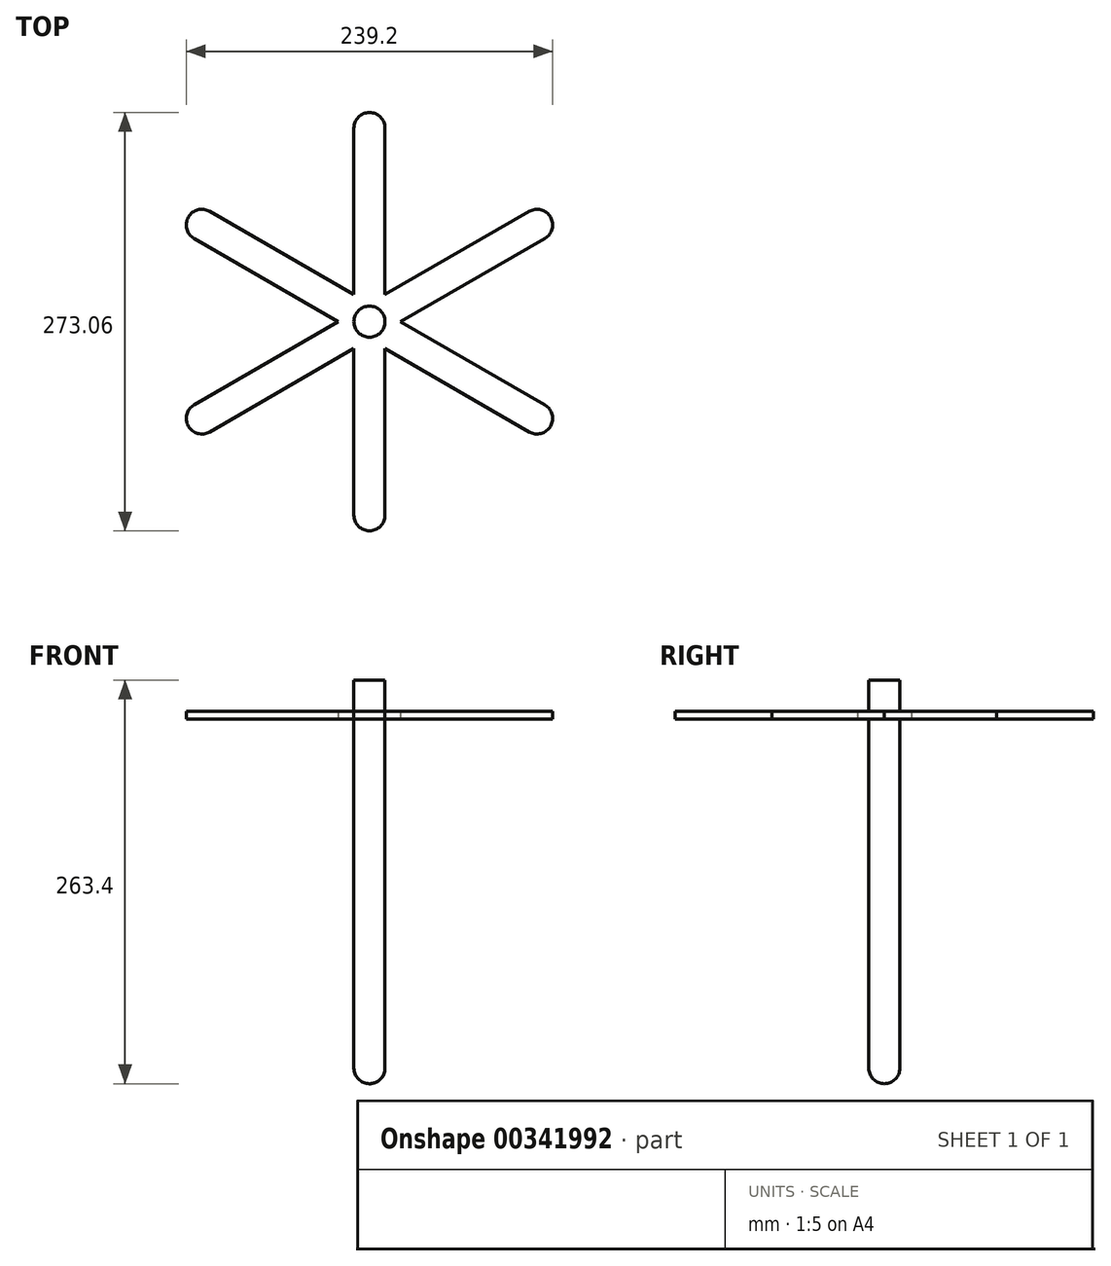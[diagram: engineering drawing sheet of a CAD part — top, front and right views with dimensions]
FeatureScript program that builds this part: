
annotation { "Feature Type Name" : "Feature", "Feature Type Description" : "" }
export const myFeature = defineFeature(function(context is Context, id is Id, definition is map)
    precondition{}
    {
        {
            var Q0;
            Q0=qCreatedBy(makeId("Top.planeOp"),FACE);
            var sketch = newSketch(context, id + "F0", { "sketchPlane" : qUnion([Q0])});
            skCircle(sketch, "E0", {"center": v(0, 0) * mm, "radius": 10.16 * mm});
            skSolve(sketch);
        }
        {
            var Q0;
            Q0=makeQuery(id+"F0.imprint","IMPRINT",FACE,{"disambiguationData":[TD([[makeQuery(id+"F0.imprint","IMPRINT",EDGE,{"derivedFrom":sQuery(id+"F0.wireOp",EDGE,"E0")}),1.0]])]});
            extrude(context, id + "F1", {"entities" : qUnion([Q0]), "depth" : 263.4 * mm});
        }
        {
            var Q0;
            Q0=makeQuery(id+"F1.opExtrude","CAP_FACE",FACE,{"disambiguationData":[OSD([sQuery(id+"F0.wireOp",EDGE,"E0")])],"isStart":false});
            cPlane(context, id + "F2", {"entities" : qUnion([Q0]), "cplaneType" : CPlaneType.OFFSET, "offset" : 25.4 * mm, "oppositeDirection" : true, "width" : 152.4 * mm, "height" : 152.4 * mm});
        }
        {
            var Q0;
            Q0=qCreatedBy(id+"F2.planeOp",FACE);
            var sketch = newSketch(context, id + "F3", { "sketchPlane" : qUnion([Q0])});
            skLineSegment(sketch, "E1.bottom", {"start": v(0, 136.53) * mm, "end": v(0, 136.53) * mm});
            skLineSegment(sketch, "E1.left", {"start": v(-10.16, 126.37) * mm, "end": v(-10.16, 17.6) * mm});
            skLineSegment(sketch, "E1.right", {"start": v(10.16, 126.37) * mm, "end": v(10.16, 17.6) * mm});
            skPoint(sketch, "E1.middle", {"position": v(0, 68.26) * mm});
            skPoint(sketch, "E2.end.orphan", {"position": v(0, 136.53) * mm});
            skPoint(sketch, "E3.visualSharp", {"position": v(-10.16, 136.53) * mm});
            skArc(sketch, "E3.filletArc", {"start": v(0, 136.53) * mm, "mid": v(-7.18, 133.55) * mm, "end": v(-10.16, 126.37) * mm});
            skPoint(sketch, "E4.visualSharp", {"position": v(10.16, 136.53) * mm});
            skArc(sketch, "E4.filletArc", {"start": v(10.16, 126.37) * mm, "mid": v(7.18, 133.55) * mm, "end": v(0, 136.53) * mm});
            skLineSegment(sketch, "E5.1.0", {"start": v(-104.36, 71.98) * mm, "end": v(-10.16, 17.6) * mm});
            skLineSegment(sketch, "E5.1.1", {"start": v(-114.52, 54.38) * mm, "end": v(-20.32, 0) * mm});
            skArc(sketch, "E5.1.2", {"start": v(-104.36, 71.98) * mm, "mid": v(-112.06, 73) * mm, "end": v(-118.23, 68.26) * mm});
            skArc(sketch, "E5.1.3", {"start": v(-118.23, 68.26) * mm, "mid": v(-119.25, 60.55) * mm, "end": v(-114.52, 54.38) * mm});
            skLineSegment(sketch, "E5.2.0", {"start": v(-114.52, -54.38) * mm, "end": v(-20.32, 0) * mm});
            skLineSegment(sketch, "E5.2.1", {"start": v(-104.36, -71.98) * mm, "end": v(-10.16, -17.6) * mm});
            skArc(sketch, "E5.2.2", {"start": v(-114.52, -54.38) * mm, "mid": v(-119.25, -60.55) * mm, "end": v(-118.23, -68.26) * mm});
            skArc(sketch, "E5.2.3", {"start": v(-118.23, -68.26) * mm, "mid": v(-112.06, -73) * mm, "end": v(-104.36, -71.98) * mm});
            skLineSegment(sketch, "E5.3.0", {"start": v(-10.16, -126.37) * mm, "end": v(-10.16, -17.6) * mm});
            skLineSegment(sketch, "E5.3.1", {"start": v(10.16, -126.37) * mm, "end": v(10.16, -17.6) * mm});
            skArc(sketch, "E5.3.2", {"start": v(-10.16, -126.37) * mm, "mid": v(-7.18, -133.55) * mm, "end": v(0, -136.53) * mm});
            skArc(sketch, "E5.3.3", {"start": v(0, -136.53) * mm, "mid": v(7.18, -133.55) * mm, "end": v(10.16, -126.37) * mm});
            skLineSegment(sketch, "E5.4.0", {"start": v(104.36, -71.98) * mm, "end": v(10.16, -17.6) * mm});
            skLineSegment(sketch, "E5.4.1", {"start": v(114.52, -54.38) * mm, "end": v(20.32, 0) * mm});
            skArc(sketch, "E5.4.2", {"start": v(104.36, -71.98) * mm, "mid": v(112.06, -73) * mm, "end": v(118.23, -68.26) * mm});
            skArc(sketch, "E5.4.3", {"start": v(118.23, -68.26) * mm, "mid": v(119.25, -60.55) * mm, "end": v(114.52, -54.38) * mm});
            skLineSegment(sketch, "E5.5.0", {"start": v(114.52, 54.38) * mm, "end": v(20.32, 0) * mm});
            skLineSegment(sketch, "E5.5.1", {"start": v(104.36, 71.98) * mm, "end": v(10.16, 17.6) * mm});
            skArc(sketch, "E5.5.2", {"start": v(114.52, 54.38) * mm, "mid": v(119.25, 60.55) * mm, "end": v(118.23, 68.26) * mm});
            skArc(sketch, "E5.5.3", {"start": v(118.23, 68.26) * mm, "mid": v(112.06, 73) * mm, "end": v(104.36, 71.98) * mm});
            skPoint(sketch, "E5.center", {"position": v(0, 0) * mm});
            skPoint(sketch, "E6.orphan", {"position": v(-5.08, -8.8) * mm});
            skPoint(sketch, "E7.orphan", {"position": v(-10.16, 0) * mm});
            skPoint(sketch, "E8.orphan", {"position": v(-5.08, 8.8) * mm});
            skPoint(sketch, "E9.orphan", {"position": v(10.16, 0) * mm});
            skSolve(sketch);
        }
        {
            var Q0;
            Q0 = qSketchRegion(id + "F3", true);
            extrude(context, id + "F4", {"entities" : qUnion([Q0]), "operationType" : NewBodyOperationType.ADD, "depth" : 5.08 * mm});
        }
        {
            var Q0;
            Q0=makeQuery(id+"F1.opExtrude","CAP_EDGE",EDGE,{"disambiguationData":[OSD([sQuery(id+"F0.wireOp",EDGE,"E0")])],"isStart":true});
            fillet(context, id + "F5", {"entities" : qUnion([Q0]), "radius" : 10.16 * mm, "tangentPropagation" : true, "allowEdgeOverflow" : false});
        }
    });
